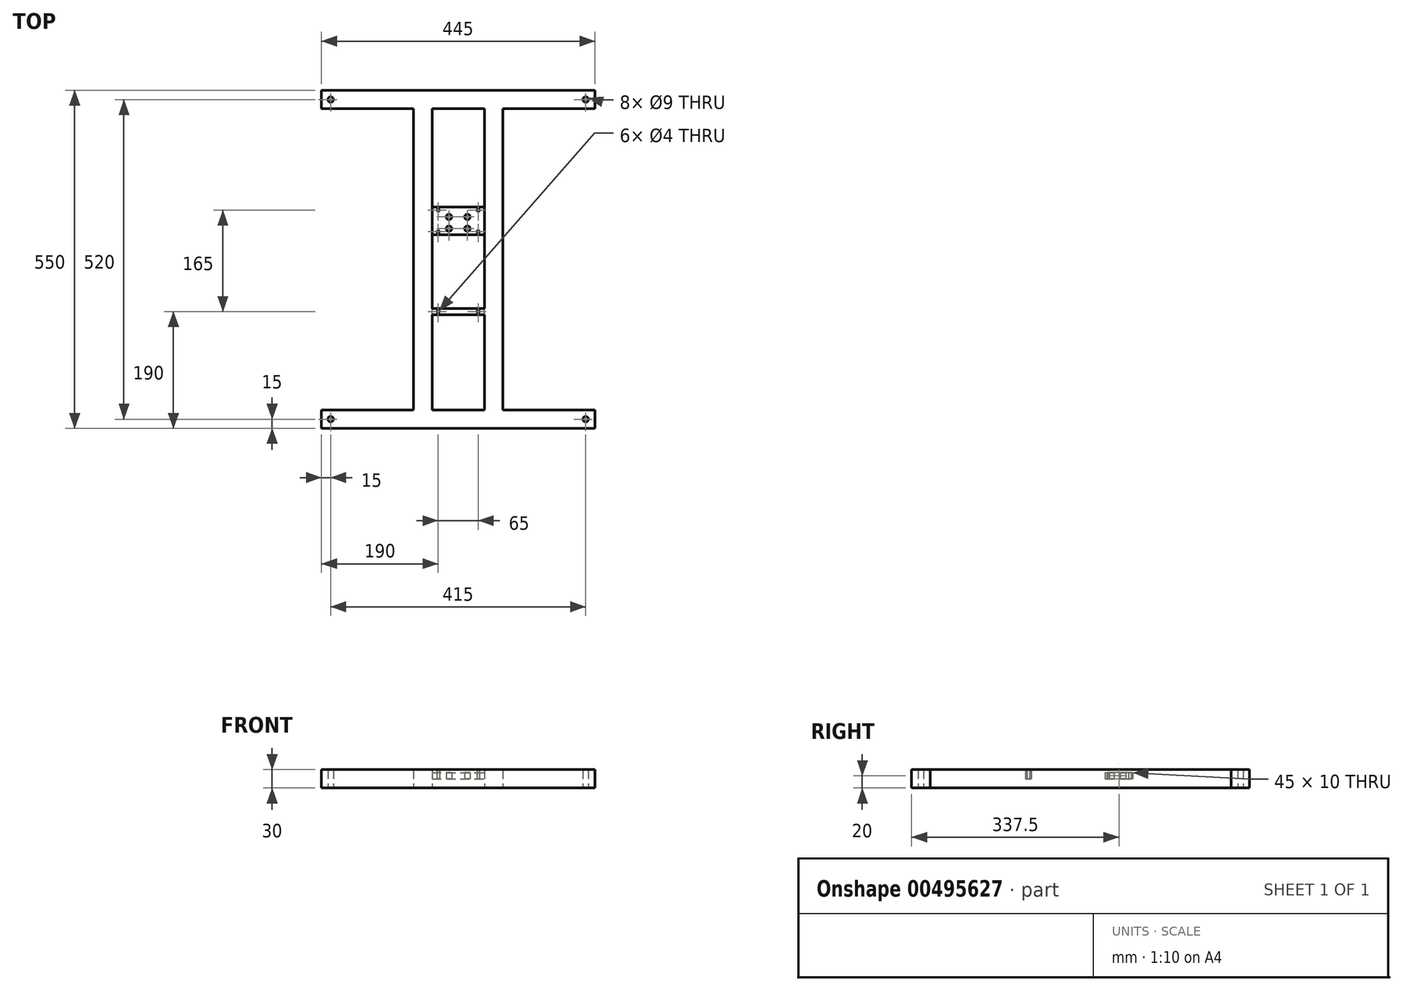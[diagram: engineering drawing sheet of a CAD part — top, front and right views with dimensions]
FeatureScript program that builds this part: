
annotation { "Feature Type Name" : "Feature", "Feature Type Description" : "" }
export const myFeature = defineFeature(function(context is Context, id is Id, definition is map)
    precondition{}
    {
        {
            var Q0;
            Q0=qCreatedBy(makeId("Top.planeOp"),FACE);
            var sketch = newSketch(context, id + "F0", { "sketchPlane" : qUnion([Q0])});
            skLineSegment(sketch, "E0.bottom", {"start": v(0, 0) * mm, "end": v(85, 0) * mm});
            skLineSegment(sketch, "E0.top", {"start": v(0, 45) * mm, "end": v(85, 45) * mm});
            skCircle(sketch, "E1", {"center": v(27.5, 29) * mm, "radius": 4.5 * mm});
            skCircle(sketch, "E2", {"center": v(57.5, 29) * mm, "radius": 4.5 * mm});
            skCircle(sketch, "E3", {"center": v(27.5, 10) * mm, "radius": 4.5 * mm});
            skCircle(sketch, "E4", {"center": v(57.5, 10) * mm, "radius": 4.5 * mm});
            skLineSegment(sketch, "E5", {"start": v(85, 45) * mm, "end": v(85, 205) * mm});
            skLineSegment(sketch, "E6", {"start": v(115, 205) * mm, "end": v(115, -285) * mm});
            skLineSegment(sketch, "E7", {"start": v(85, -285) * mm, "end": v(85, 0) * mm});
            skLineSegment(sketch, "E8", {"start": v(0, 45) * mm, "end": v(0, 205) * mm});
            skLineSegment(sketch, "E9", {"start": v(-30, 205) * mm, "end": v(-30, -285) * mm});
            skLineSegment(sketch, "E10", {"start": v(0, -285) * mm, "end": v(0, 0) * mm});
            skLineSegment(sketch, "E11", {"start": v(115, 205) * mm, "end": v(265, 205) * mm});
            skLineSegment(sketch, "E12", {"start": v(265, 205) * mm, "end": v(265, 235) * mm});
            skLineSegment(sketch, "E13", {"start": v(265, 235) * mm, "end": v(-180, 235) * mm});
            skLineSegment(sketch, "E14", {"start": v(-180, 235) * mm, "end": v(-180, 205) * mm});
            skLineSegment(sketch, "E15", {"start": v(85, 205) * mm, "end": v(0, 205) * mm});
            skLineSegment(sketch, "E16", {"start": v(-30, 205) * mm, "end": v(-180, 205) * mm});
            skLineSegment(sketch, "E17", {"start": v(-30, -285) * mm, "end": v(-180, -285) * mm});
            skLineSegment(sketch, "E18", {"start": v(-180, -285) * mm, "end": v(-180, -315) * mm});
            skLineSegment(sketch, "E19", {"start": v(-180, -315) * mm, "end": v(265, -315) * mm});
            skLineSegment(sketch, "E20", {"start": v(265, -315) * mm, "end": v(265, -285) * mm});
            skLineSegment(sketch, "E21", {"start": v(265, -285) * mm, "end": v(115, -285) * mm});
            skLineSegment(sketch, "E22", {"start": v(85, -285) * mm, "end": v(0, -285) * mm});
            skCircle(sketch, "E23", {"center": v(-165, 220) * mm, "radius": 4.5 * mm});
            skCircle(sketch, "E24", {"center": v(250, 220) * mm, "radius": 4.5 * mm});
            skCircle(sketch, "E25", {"center": v(250, -300) * mm, "radius": 4.5 * mm});
            skCircle(sketch, "E26", {"center": v(-165, -300) * mm, "radius": 4.5 * mm});
            skLineSegment(sketch, "E27.bottom", {"start": v(0, -120) * mm, "end": v(85, -120) * mm});
            skLineSegment(sketch, "E27.top", {"start": v(0, -130) * mm, "end": v(85, -130) * mm});
            skLineSegment(sketch, "E27.left", {"start": v(0, -120) * mm, "end": v(0, -130) * mm});
            skLineSegment(sketch, "E27.right", {"start": v(85, -120) * mm, "end": v(85, -130) * mm});
            skCircle(sketch, "E28", {"center": v(10, -125) * mm, "radius": 2 * mm});
            skCircle(sketch, "E29", {"center": v(75, -125) * mm, "radius": 2 * mm});
            skSolve(sketch);
        }
        {
            var Q0;
            Q0=makeQuery(id+"F0.imprint","IMPRINT",FACE,{"disambiguationData":[TD([[makeQuery(id+"F0.imprint","IMPRINT",EDGE,{"derivedFrom":sQuery(id+"F0.wireOp",EDGE,"E0.bottom")}),1.0]])]});
            var Q1;
            Q1=makeQuery(id+"F0.imprint","IMPRINT",FACE,{"disambiguationData":[TD([[makeQuery(id+"F0.imprint","IMPRINT",EDGE,{"derivedFrom":sQuery(id+"F0.wireOp",EDGE,"E27.bottom")}),-1.0]])]});
            extrude(context, id + "F1", {"entities" : qUnion([Q0, Q1]), "depth" : 30 * mm});
        }
        {
            var Q0;
            Q0=makeQuery(id+"F1.opExtrude","CAP_FACE",FACE,{"disambiguationData":[OSD([sQuery(id+"F0.wireOp",EDGE,"E0.bottom"),sQuery(id+"F0.wireOp",EDGE,"E0.top"),sQuery(id+"F0.wireOp",EDGE,"E1"),sQuery(id+"F0.wireOp",EDGE,"E2"),sQuery(id+"F0.wireOp",EDGE,"E3"),sQuery(id+"F0.wireOp",EDGE,"E4"),sQuery(id+"F0.wireOp",EDGE,"E5"),sQuery(id+"F0.wireOp",EDGE,"E6"),sQuery(id+"F0.wireOp",EDGE,"E7"),sQuery(id+"F0.wireOp",EDGE,"E8"),sQuery(id+"F0.wireOp",EDGE,"E9"),sQuery(id+"F0.wireOp",EDGE,"E10"),sQuery(id+"F0.wireOp",EDGE,"E11"),sQuery(id+"F0.wireOp",EDGE,"E12"),sQuery(id+"F0.wireOp",EDGE,"E13"),sQuery(id+"F0.wireOp",EDGE,"E14"),sQuery(id+"F0.wireOp",EDGE,"E15"),sQuery(id+"F0.wireOp",EDGE,"E16"),sQuery(id+"F0.wireOp",EDGE,"E17"),sQuery(id+"F0.wireOp",EDGE,"E18"),sQuery(id+"F0.wireOp",EDGE,"E19"),sQuery(id+"F0.wireOp",EDGE,"E20"),sQuery(id+"F0.wireOp",EDGE,"E21"),sQuery(id+"F0.wireOp",EDGE,"E22")])],"isStart":false});
            var sketch = newSketch(context, id + "F2", { "sketchPlane" : qUnion([Q0])});
            skLineSegment(sketch, "E30.bottom", {"start": v(0, 45) * mm, "end": v(85, 45) * mm});
            skLineSegment(sketch, "E30.top", {"start": v(0, 0) * mm, "end": v(85, 0) * mm});
            skLineSegment(sketch, "E30.left", {"start": v(0, 45) * mm, "end": v(0, 0) * mm});
            skLineSegment(sketch, "E30.right", {"start": v(85, 45) * mm, "end": v(85, 0) * mm});
            skLineSegment(sketch, "E31.bottom", {"start": v(0, 40) * mm, "end": v(85, 40) * mm});
            skLineSegment(sketch, "E31.left", {"start": v(0, 40) * mm, "end": v(0, 45) * mm});
            skLineSegment(sketch, "E31.right", {"start": v(85, 40) * mm, "end": v(85, 45) * mm});
            skSolve(sketch);
        }
        {
            var Q0;
            Q0=makeQuery(id+"F2.imprint","IMPRINT",FACE,{"disambiguationData":[TD([[makeQuery(id+"F2.imprint","IMPRINT",EDGE,{"derivedFrom":sQuery(id+"F2.wireOp",EDGE,"E30.top")}),1.0]])]});
            var Q1;
            Q1=makeQuery(id+"F2.imprint","IMPRINT",FACE,{"disambiguationData":[TD([[makeQuery(id+"F2.imprint","IMPRINT",EDGE,{"derivedFrom":sQuery(id+"F2.wireOp",EDGE,"E31.bottom")}),1.0]])]});
            extrude(context, id + "F3", {"entities" : qUnion([Q0, Q1]), "operationType" : NewBodyOperationType.REMOVE, "oppositeDirection" : true, "depth" : 5 * mm});
        }
        {
            var Q0;
            Q0=makeQuery(id+"F0.imprint","IMPRINT",FACE,{"disambiguationData":[TD([[makeQuery(id+"F0.imprint","IMPRINT",EDGE,{"derivedFrom":sQuery(id+"F0.wireOp",EDGE,"E0.bottom")}),1.0]])]});
            var sketch = newSketch(context, id + "F4", { "sketchPlane" : qUnion([Q0])});
            skLineSegment(sketch, "E32.bottom", {"start": v(0, 0) * mm, "end": v(85, 0) * mm});
            skLineSegment(sketch, "E32.top", {"start": v(0, 45) * mm, "end": v(85, 45) * mm});
            skLineSegment(sketch, "E32.left", {"start": v(0, 0) * mm, "end": v(0, 45) * mm});
            skLineSegment(sketch, "E32.right", {"start": v(85, 0) * mm, "end": v(85, 45) * mm});
            skCircle(sketch, "E33", {"center": v(27.5, 10) * mm, "radius": 6 * mm});
            skCircle(sketch, "E34", {"center": v(57.5, 10) * mm, "radius": 6 * mm});
            skCircle(sketch, "E35", {"center": v(27.5, 29) * mm, "radius": 6 * mm});
            skCircle(sketch, "E36", {"center": v(57.5, 29) * mm, "radius": 6 * mm});
            skCircle(sketch, "E37", {"center": v(10, 5) * mm, "radius": 2 * mm});
            skCircle(sketch, "E38", {"center": v(75, 5) * mm, "radius": 2 * mm});
            skCircle(sketch, "E39", {"center": v(75, 40) * mm, "radius": 2 * mm});
            skCircle(sketch, "E40", {"center": v(10, 40) * mm, "radius": 2 * mm});
            skSolve(sketch);
        }
        {
            var Q0;
            Q0=makeQuery(id+"F4.imprint","IMPRINT",FACE,{"disambiguationData":[TD([[makeQuery(id+"F4.imprint","IMPRINT",EDGE,{"derivedFrom":sQuery(id+"F4.wireOp",EDGE,"E32.bottom")}),1.0]])]});
            var Q1;
            Q1=makeQuery(id+"F0.imprint","IMPRINT",FACE,{"disambiguationData":[TD([[makeQuery(id+"F0.imprint","IMPRINT",EDGE,{"derivedFrom":sQuery(id+"F0.wireOp",EDGE,"E27.bottom")}),-1.0]])]});
            extrude(context, id + "F5", {"entities" : qUnion([Q0, Q1]), "operationType" : NewBodyOperationType.REMOVE, "depth" : 15 * mm});
        }
        {
            var Q0;
            Q0=makeQuery(id+"F4.imprint","IMPRINT",FACE,{"disambiguationData":[TD([[makeQuery(id+"F4.imprint","IMPRINT",EDGE,{"derivedFrom":sQuery(id+"F4.wireOp",EDGE,"E33")}),1.0]])]});
            var Q1;
            Q1=makeQuery(id+"F4.imprint","IMPRINT",FACE,{"disambiguationData":[TD([[makeQuery(id+"F4.imprint","IMPRINT",EDGE,{"derivedFrom":sQuery(id+"F4.wireOp",EDGE,"E34")}),1.0]])]});
            var Q2;
            Q2=makeQuery(id+"F4.imprint","IMPRINT",FACE,{"disambiguationData":[TD([[makeQuery(id+"F4.imprint","IMPRINT",EDGE,{"derivedFrom":sQuery(id+"F4.wireOp",EDGE,"E36")}),1.0]])]});
            var Q3;
            Q3=makeQuery(id+"F4.imprint","IMPRINT",FACE,{"disambiguationData":[TD([[makeQuery(id+"F4.imprint","IMPRINT",EDGE,{"derivedFrom":sQuery(id+"F4.wireOp",EDGE,"E35")}),1.0]])]});
            extrude(context, id + "F6", {"entities" : qUnion([Q0, Q1, Q2, Q3]), "operationType" : NewBodyOperationType.REMOVE, "depth" : 15 * mm});
        }
        {
            var Q0;
            Q0=makeQuery(id+"F4.imprint","IMPRINT",FACE,{"disambiguationData":[TD([[makeQuery(id+"F4.imprint","IMPRINT",EDGE,{"derivedFrom":sQuery(id+"F4.wireOp",EDGE,"E37")}),1.0]])]});
            var Q1;
            Q1=makeQuery(id+"F4.imprint","IMPRINT",FACE,{"disambiguationData":[TD([[makeQuery(id+"F4.imprint","IMPRINT",EDGE,{"derivedFrom":sQuery(id+"F4.wireOp",EDGE,"E40")}),1.0]])]});
            var Q2;
            Q2=makeQuery(id+"F4.imprint","IMPRINT",FACE,{"disambiguationData":[TD([[makeQuery(id+"F4.imprint","IMPRINT",EDGE,{"derivedFrom":sQuery(id+"F4.wireOp",EDGE,"E39")}),1.0]])]});
            var Q3;
            Q3=makeQuery(id+"F4.imprint","IMPRINT",FACE,{"disambiguationData":[TD([[makeQuery(id+"F4.imprint","IMPRINT",EDGE,{"derivedFrom":sQuery(id+"F4.wireOp",EDGE,"E38")}),1.0]])]});
            extrude(context, id + "F7", {"entities" : qUnion([Q0, Q1, Q2, Q3]), "operationType" : NewBodyOperationType.REMOVE, "depth" : 25 * mm});
        }
    });
